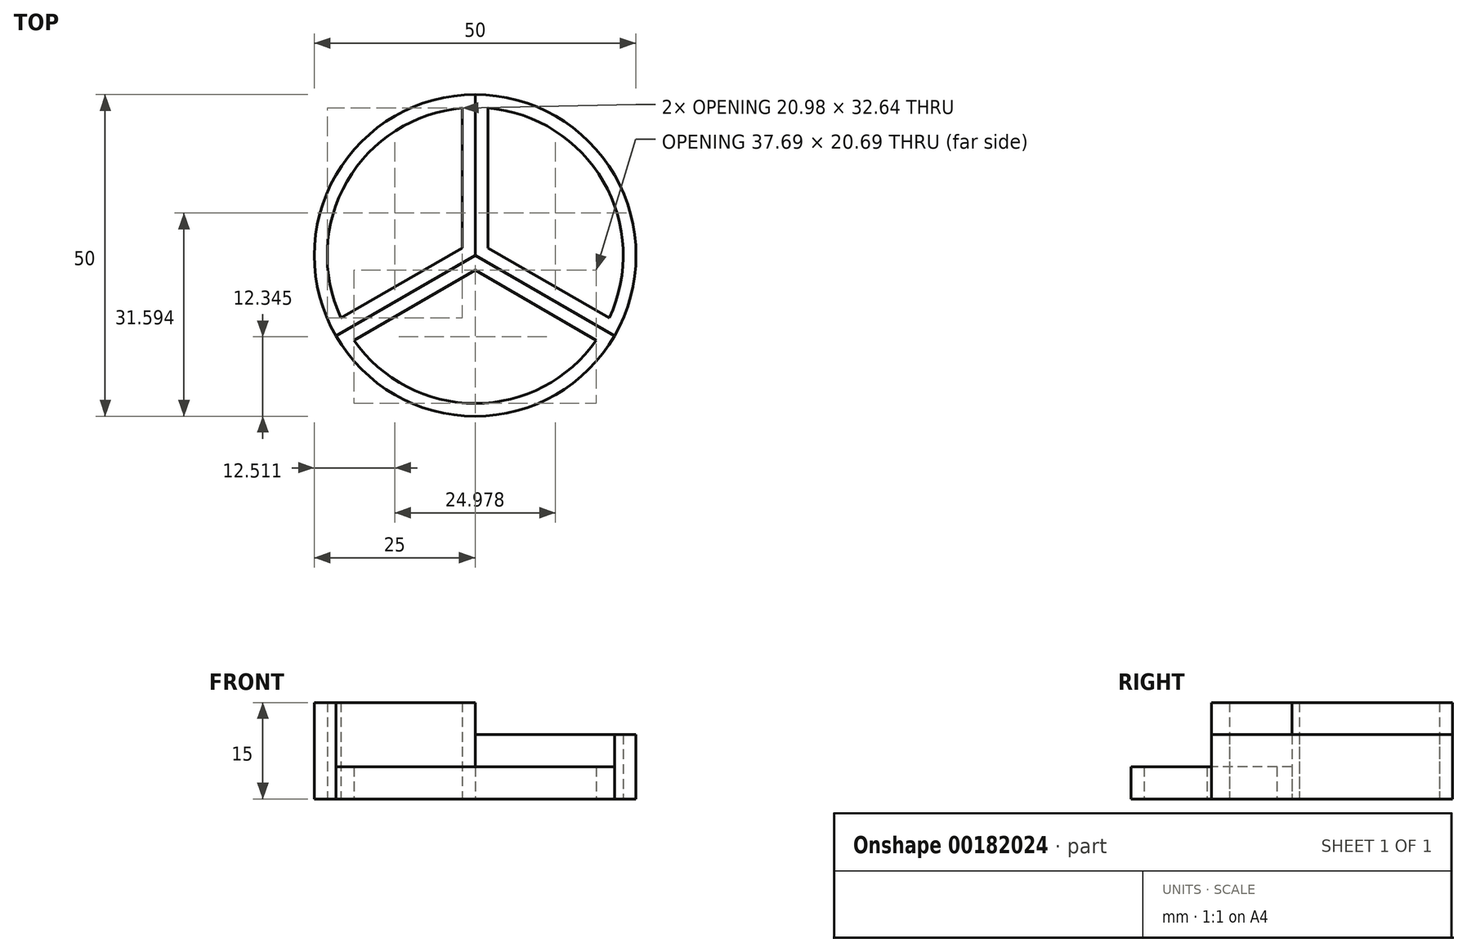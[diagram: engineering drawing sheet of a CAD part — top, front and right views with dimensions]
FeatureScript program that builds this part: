
annotation { "Feature Type Name" : "Feature", "Feature Type Description" : "" }
export const myFeature = defineFeature(function(context is Context, id is Id, definition is map)
    precondition{}
    {
        {
            var Q0;
            Q0=qCreatedBy(makeId("Top.planeOp"),FACE);
            var sketch = newSketch(context, id + "F0", { "sketchPlane" : qUnion([Q0])});
            skCircle(sketch, "E0", {"center": v(0, 0) * mm, "radius": 25 * mm});
            skLineSegment(sketch, "E1", {"start": v(0, 0) * mm, "end": v(0, 25) * mm});
            skLineSegment(sketch, "E2.1.0", {"start": v(0, 0) * mm, "end": v(-21.65, -12.5) * mm});
            skLineSegment(sketch, "E2.2.0", {"start": v(0, 0) * mm, "end": v(21.65, -12.5) * mm});
            skSolve(sketch);
        }
        {
            var Q0;
            {var subQ0=sQuery(id+"F0.wireOp",EDGE,"E1");Q0=makeQuery(id+"F0.imprint","IMPRINT",FACE,{"disambiguationData":[TD([[makeQuery(id+"F0.imprint","IMPRINT",EDGE,{"derivedFrom":subQ0}),1.0]])]});}
            extrude(context, id + "F1", {"entities" : qUnion([Q0]), "depth" : 15 * mm});
        }
        {
            var Q0;
            {var subQ0=sQuery(id+"F0.wireOp",EDGE,"E1");Q0=makeQuery(id+"F0.imprint","IMPRINT",FACE,{"disambiguationData":[TD([[makeQuery(id+"F0.imprint","IMPRINT",EDGE,{"derivedFrom":subQ0}),-1.0]])]});}
            extrude(context, id + "F2", {"entities" : qUnion([Q0]), "depth" : 10 * mm});
        }
        {
            var Q0;
            {var subQ0=sQuery(id+"F0.wireOp",EDGE,"E2.1.0");Q0=makeQuery(id+"F0.imprint","IMPRINT",FACE,{"disambiguationData":[TD([[makeQuery(id+"F0.imprint","IMPRINT",EDGE,{"derivedFrom":subQ0}),1.0]])]});}
            extrude(context, id + "F3", {"entities" : qUnion([Q0]), "depth" : 5 * mm});
        }
        {
            var Q0;
            Q0=makeQuery(id+"F1.opExtrude","CAP_FACE",FACE,{"disambiguationData":[OSD([sQuery(id+"F0.wireOp",EDGE,"E0"),sQuery(id+"F0.wireOp",EDGE,"E1"),sQuery(id+"F0.wireOp",EDGE,"E2.1.0")])],"isStart":false});
            var Q1;
            Q1=makeQuery(id+"F2.opExtrude","CAP_FACE",FACE,{"disambiguationData":[OSD([sQuery(id+"F0.wireOp",EDGE,"E0"),sQuery(id+"F0.wireOp",EDGE,"E1"),sQuery(id+"F0.wireOp",EDGE,"E2.2.0")])],"isStart":false});
            var Q2;
            Q2=makeQuery(id+"F3.opExtrude","CAP_FACE",FACE,{"disambiguationData":[OSD([sQuery(id+"F0.wireOp",EDGE,"E0"),sQuery(id+"F0.wireOp",EDGE,"E2.1.0"),sQuery(id+"F0.wireOp",EDGE,"E2.2.0")])],"isStart":false});
            shell(context, id + "F4", {"entities" : qUnion([Q0, Q1, Q2]), "thickness" : 2 * mm});
        }
        {
            var Q0;
            Q0=makeQuery(id+"F4.opShell","OFFSET_FACE",FACE,{"disambiguationData":[OSD([sQuery(id+"F0.wireOp",EDGE,"E0"),sQuery(id+"F0.wireOp",EDGE,"E1"),sQuery(id+"F0.wireOp",EDGE,"E2.1.0")])]});
            var Q1;
            Q1=makeQuery(id+"F4.opShell","OFFSET_FACE",FACE,{"disambiguationData":[OSD([sQuery(id+"F0.wireOp",EDGE,"E0"),sQuery(id+"F0.wireOp",EDGE,"E1"),sQuery(id+"F0.wireOp",EDGE,"E2.2.0")])]});
            var Q2;
            Q2=makeQuery(id+"F4.opShell","OFFSET_FACE",FACE,{"disambiguationData":[OSD([sQuery(id+"F0.wireOp",EDGE,"E0"),sQuery(id+"F0.wireOp",EDGE,"E2.1.0"),sQuery(id+"F0.wireOp",EDGE,"E2.2.0")])]});
            extrude(context, id + "F5", {"entities" : qUnion([Q0, Q1, Q2]), "operationType" : NewBodyOperationType.REMOVE, "oppositeDirection" : true, "depth" : 25 * mm});
        }
    });
